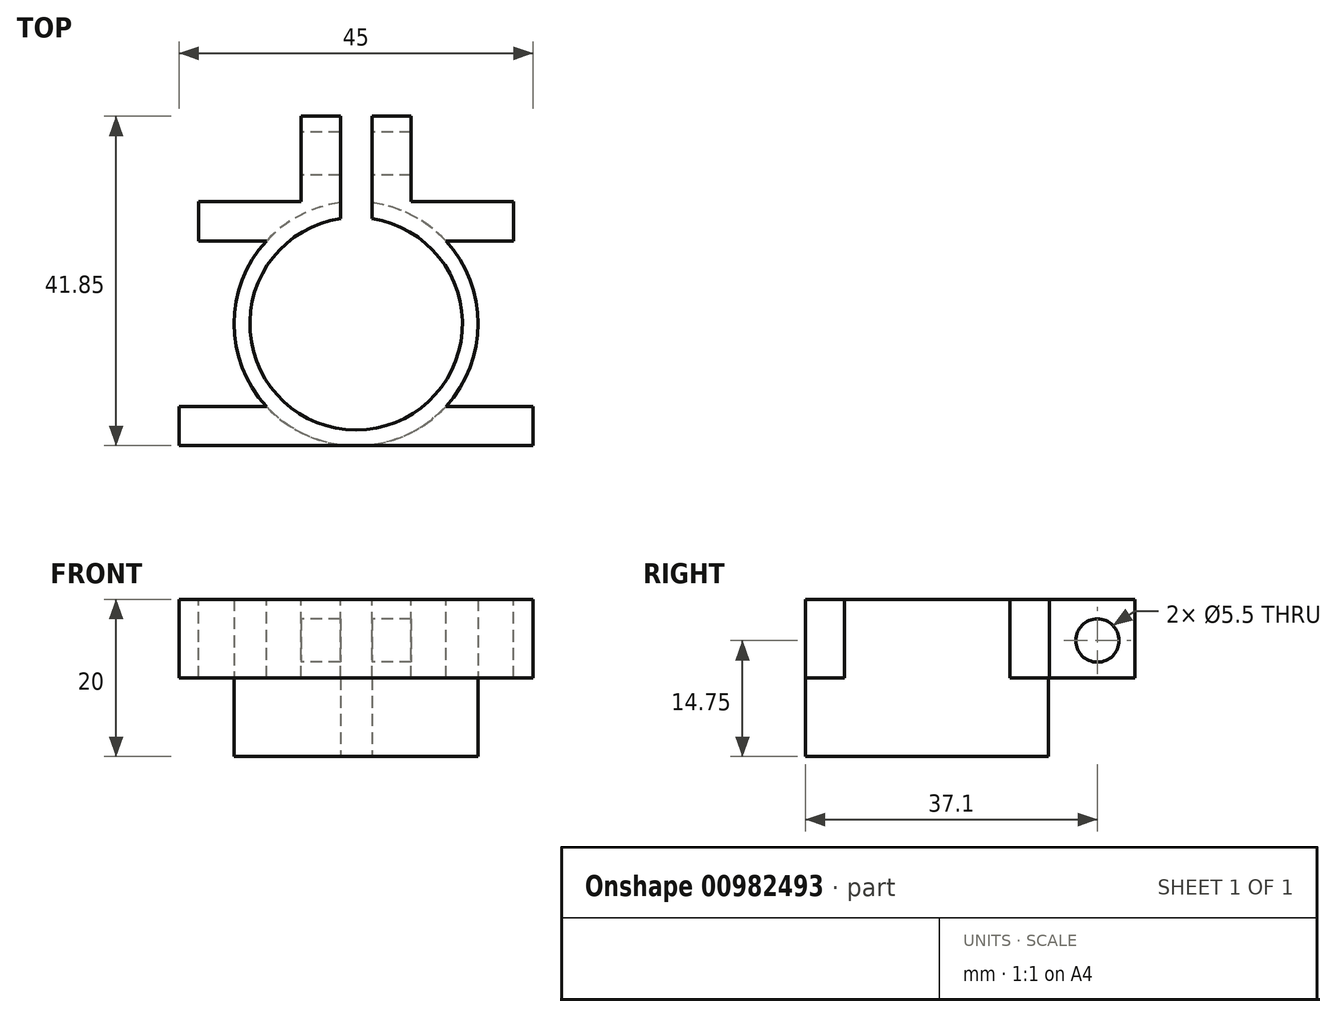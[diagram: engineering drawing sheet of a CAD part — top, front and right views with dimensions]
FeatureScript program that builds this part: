
annotation { "Feature Type Name" : "Feature", "Feature Type Description" : "" }
export const myFeature = defineFeature(function(context is Context, id is Id, definition is map)
    precondition{}
    {
        {
            var Q0;
            Q0=qCreatedBy(makeId("Top.planeOp"),FACE);
            var sketch = newSketch(context, id + "F0", { "sketchPlane" : qUnion([Q0])});
            skCircle(sketch, "E0", {"center": v(-43.3, 10.9) * mm, "radius": 13.5 * mm});
            skCircle(sketch, "E1", {"center": v(-43.3, 10.9) * mm, "radius": 15.5 * mm});
            skSolve(sketch);
        }
        {
            var Q0;
            Q0=makeQuery(id+"F0.imprint","IMPRINT",FACE,{"disambiguationData":[TD([[makeQuery(id+"F0.imprint","IMPRINT",EDGE,{"derivedFrom":sQuery(id+"F0.wireOp",EDGE,"E0")}),-1.0]])]});
            extrude(context, id + "F1", {"entities" : qUnion([Q0]), "depth" : 20 * mm, "offsetDistance" : 25 * mm});
        }
        {
            var Q0;
            Q0=makeQuery(id+"F1.opExtrude","CAP_FACE",FACE,{"disambiguationData":[OSD([sQuery(id+"F0.wireOp",EDGE,"E0"),sQuery(id+"F0.wireOp",EDGE,"E1")])],"isStart":false});
            var sketch = newSketch(context, id + "F2", { "sketchPlane" : qUnion([Q0])});
            skLineSegment(sketch, "E2.bottom", {"start": v(-45.3, 37.25) * mm, "end": v(-50.3, 37.25) * mm});
            skLineSegment(sketch, "E2.top", {"start": v(-45.3, 24.25) * mm, "end": v(-50.3, 24.25) * mm});
            skLineSegment(sketch, "E2.left", {"start": v(-45.3, 37.25) * mm, "end": v(-45.3, 24.25) * mm});
            skLineSegment(sketch, "E2.right", {"start": v(-50.3, 37.25) * mm, "end": v(-50.3, 24.25) * mm});
            skLineSegment(sketch, "E3", {"start": v(-43.3, 36.04) * mm, "end": v(-43.3, 6.76) * mm});
            skLineSegment(sketch, "E4.MirrorCS", {"start": v(-41.3, 24.25) * mm, "end": v(-36.3, 24.25) * mm});
            skLineSegment(sketch, "E5.MirrorCS", {"start": v(-36.3, 37.25) * mm, "end": v(-36.3, 24.25) * mm});
            skLineSegment(sketch, "E6.MirrorCS", {"start": v(-41.3, 37.25) * mm, "end": v(-41.3, 24.25) * mm});
            skLineSegment(sketch, "E7.MirrorCS", {"start": v(-41.3, 37.25) * mm, "end": v(-36.3, 37.25) * mm});
            skPoint(sketch, "E8.oppositeSnap0", {"position": v(-43.3, 21.4) * mm});
            skLineSegment(sketch, "E8.bottom", {"start": v(-63.3, 26.4) * mm, "end": v(-23.3, 26.4) * mm});
            skLineSegment(sketch, "E8.top", {"start": v(-63.3, 21.4) * mm, "end": v(-23.3, 21.4) * mm});
            skLineSegment(sketch, "E8.left", {"start": v(-63.3, 26.4) * mm, "end": v(-63.3, 21.4) * mm});
            skLineSegment(sketch, "E8.right", {"start": v(-23.3, 26.4) * mm, "end": v(-23.3, 21.4) * mm});
            skLineSegment(sketch, "E9.bottom", {"start": v(-65.8, 0.4) * mm, "end": v(-20.8, 0.4) * mm});
            skLineSegment(sketch, "E9.top", {"start": v(-65.8, -4.6) * mm, "end": v(-20.8, -4.6) * mm});
            skLineSegment(sketch, "E9.left", {"start": v(-65.8, 0.4) * mm, "end": v(-65.8, -4.6) * mm});
            skLineSegment(sketch, "E9.right", {"start": v(-20.8, 0.4) * mm, "end": v(-20.8, -4.6) * mm});
            skLineSegment(sketch, "E10", {"start": v(-74.07, 10.9) * mm, "end": v(-17.4, 10.9) * mm});
            skSolve(sketch);
        }
        {
            var Q0;
            {var subQ0=sQuery(id+"F2.wireOp",EDGE,"E2.bottom");Q0=makeQuery(id+"F2.imprint","IMPRINT",FACE,{"disambiguationData":[TD([[makeQuery(id+"F2.imprint","IMPRINT",EDGE,{"derivedFrom":subQ0}),1.0]])]});}
            var Q1;
            {var subQ0=sQuery(id+"F2.wireOp",EDGE,"E7.MirrorCS");Q1=makeQuery(id+"F2.imprint","IMPRINT",FACE,{"disambiguationData":[TD([[makeQuery(id+"F2.imprint","IMPRINT",EDGE,{"derivedFrom":subQ0}),-1.0]])]});}
            var Q2;
            {var subQ0=sQuery(id+"F2.wireOp",EDGE,"E8.left");Q2=makeQuery(id+"F2.imprint","IMPRINT",FACE,{"disambiguationData":[TD([[makeQuery(id+"F2.imprint","IMPRINT",EDGE,{"derivedFrom":subQ0}),1.0]])]});}
            var Q3;
            {var subQ0=sQuery(id+"F2.wireOp",EDGE,"E8.right");Q3=makeQuery(id+"F2.imprint","IMPRINT",FACE,{"disambiguationData":[TD([[makeQuery(id+"F2.imprint","IMPRINT",EDGE,{"derivedFrom":subQ0}),-1.0]])]});}
            var Q4;
            {var subQ0=sQuery(id+"F2.wireOp",EDGE,"E8.bottom");var subQ1=sQuery(id+"F2.wireOp",EDGE,"E2.right");var subQ2=makeQuery(id+"F2.imprint","INTERSECT",VERTEX,{"derivedFrom":[subQ1,subQ0]});Q4=makeQuery(id+"F2.imprint","IMPRINT",FACE,{"disambiguationData":[TD([[makeQuery(id+"F2.imprint","IMPRINT",EDGE,{"disambiguationData":[TD([[subQ2,-1.0]])],"derivedFrom":subQ1}),1.0]])]});}
            var Q5;
            {var subQ0=sQuery(id+"F2.wireOp",EDGE,"E8.bottom");var subQ1=sQuery(id+"F2.wireOp",EDGE,"E5.MirrorCS");var subQ2=makeQuery(id+"F2.imprint","INTERSECT",VERTEX,{"derivedFrom":[subQ1,subQ0]});Q5=makeQuery(id+"F2.imprint","IMPRINT",FACE,{"disambiguationData":[TD([[makeQuery(id+"F2.imprint","IMPRINT",EDGE,{"disambiguationData":[TD([[subQ2,-1.0]])],"derivedFrom":subQ1}),-1.0]])]});}
            var Q6;
            {var subQ0=sQuery(id+"F2.wireOp",EDGE,"E9.left");Q6=makeQuery(id+"F2.imprint","IMPRINT",FACE,{"disambiguationData":[TD([[makeQuery(id+"F2.imprint","IMPRINT",EDGE,{"derivedFrom":subQ0}),1.0]])]});}
            var Q7;
            {var subQ0=sQuery(id+"F2.wireOp",EDGE,"E9.right");Q7=makeQuery(id+"F2.imprint","IMPRINT",FACE,{"disambiguationData":[TD([[makeQuery(id+"F2.imprint","IMPRINT",EDGE,{"derivedFrom":subQ0}),-1.0]])]});}
            extrude(context, id + "F3", {"entities" : qUnion([Q0, Q1, Q2, Q3, Q4, Q5, Q6, Q7]), "operationType" : NewBodyOperationType.ADD, "oppositeDirection" : true, "depth" : 10 * mm, "offsetDistance" : 25 * mm});
        }
        {
            var Q0;
            {var subQ0=sQuery(id+"F0.wireOp",EDGE,"E1");Q0=makeQuery(id+"F3.boolean.opBoolean","MERGE",FACE,{"derivedFrom":[makeQuery(id+"F1.opExtrude","CAP_FACE",FACE,{"disambiguationData":[OSD([sQuery(id+"F0.wireOp",EDGE,"E0"),subQ0])],"isStart":false}),makeQuery(id+"F3.opExtrude","CAP_FACE",FACE,{"disambiguationData":[OSD([subQ0,sQuery(id+"F2.wireOp",EDGE,"E2.bottom"),sQuery(id+"F2.wireOp",EDGE,"E2.left"),sQuery(id+"F2.wireOp",EDGE,"E2.right")])],"isStart":true}),makeQuery(id+"F3.opExtrude","CAP_FACE",FACE,{"disambiguationData":[OSD([subQ0,sQuery(id+"F2.wireOp",EDGE,"E5.MirrorCS"),sQuery(id+"F2.wireOp",EDGE,"E6.MirrorCS"),sQuery(id+"F2.wireOp",EDGE,"E7.MirrorCS")])],"isStart":true})]});}
            var sketch = newSketch(context, id + "F4", { "sketchPlane" : qUnion([Q0])});
            skLineSegment(sketch, "E11.bottom", {"start": v(-45.3, 27.5) * mm, "end": v(-41.3, 27.5) * mm});
            skLineSegment(sketch, "E11.top", {"start": v(-45.3, 24.25) * mm, "end": v(-41.3, 24.25) * mm});
            skLineSegment(sketch, "E11.left", {"start": v(-45.3, 27.5) * mm, "end": v(-45.3, 24.25) * mm});
            skLineSegment(sketch, "E11.right", {"start": v(-41.3, 27.5) * mm, "end": v(-41.3, 24.25) * mm});
            skSolve(sketch);
        }
        {
            var Q0;
            {var subQ11=sQuery(id+"F4.wireOp",EDGE,"E11.right");Q0=makeQuery(id+"F4.imprint","IMPRINT",FACE,{"disambiguationData":[TD([[makeQuery(id+"F4.imprint","IMPRINT",EDGE,{"derivedFrom":subQ11}),-1.0]])]});}
            extrude(context, id + "F5", {"entities" : qUnion([Q0]), "operationType" : NewBodyOperationType.REMOVE, "oppositeDirection" : true, "depth" : 25 * mm, "offsetDistance" : 25 * mm});
        }
        {
            var Q0;
            Q0=makeQuery(id+"F3.opExtrude","SWEPT_FACE",FACE,{"disambiguationData":[OSD([sQuery(id+"F2.wireOp",EDGE,"E2.right")])]});
            var sketch = newSketch(context, id + "F6", { "sketchPlane" : qUnion([Q0])});
            skCircle(sketch, "E12", {"center": v(-32.5, 14.75) * mm, "radius": 2.75 * mm});
            skSolve(sketch);
        }
        {
            var Q0;
            Q0=makeQuery(id+"F6.imprint","IMPRINT",FACE,{"disambiguationData":[TD([[makeQuery(id+"F6.imprint","IMPRINT",EDGE,{"derivedFrom":sQuery(id+"F6.wireOp",EDGE,"E12")}),1.0]])]});
            extrude(context, id + "F7", {"entities" : qUnion([Q0]), "operationType" : NewBodyOperationType.REMOVE, "oppositeDirection" : true, "depth" : 15 * mm, "offsetDistance" : 25 * mm});
        }
    });
